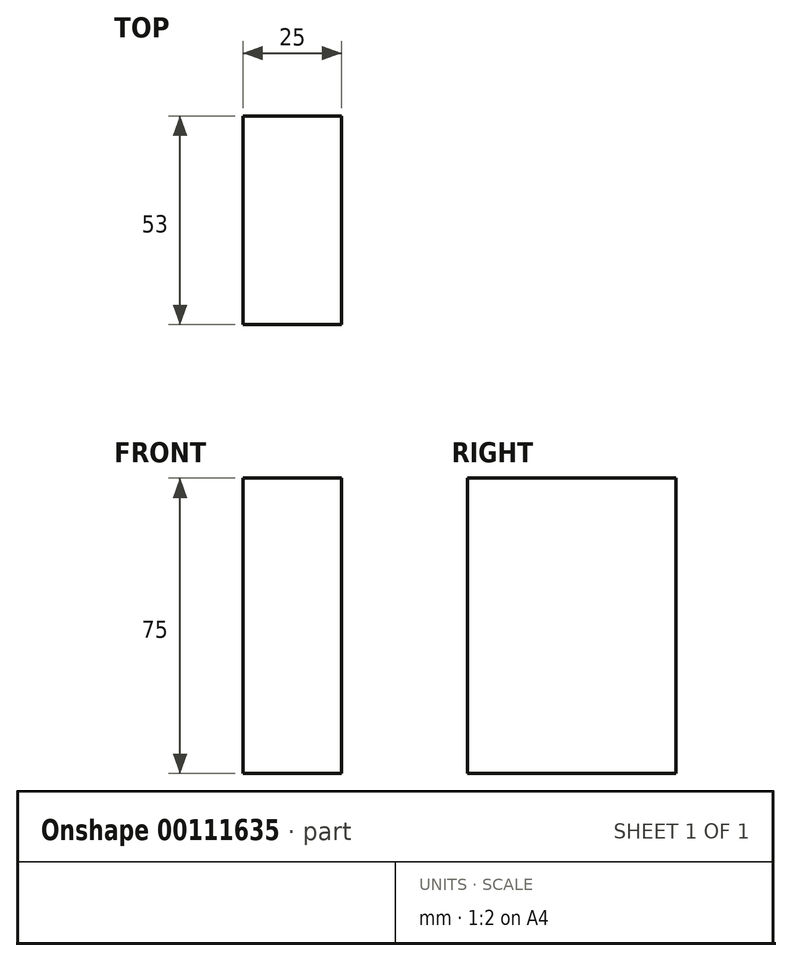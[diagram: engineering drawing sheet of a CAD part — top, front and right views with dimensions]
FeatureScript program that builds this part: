
annotation { "Feature Type Name" : "Feature", "Feature Type Description" : "" }
export const myFeature = defineFeature(function(context is Context, id is Id, definition is map)
    precondition{}
    {
        {
            var Q0;
            Q0=qCreatedBy(makeId("Front.planeOp"),FACE);
            var sketch = newSketch(context, id + "F0", { "sketchPlane" : qUnion([Q0])});
            skLineSegment(sketch, "E0.bottom", {"start": v(12.5, -37.5) * mm, "end": v(-12.5, -37.5) * mm});
            skLineSegment(sketch, "E0.top", {"start": v(12.5, 37.5) * mm, "end": v(-12.5, 37.5) * mm});
            skLineSegment(sketch, "E0.left", {"start": v(12.5, -37.5) * mm, "end": v(12.5, 37.5) * mm});
            skLineSegment(sketch, "E0.right", {"start": v(-12.5, -37.5) * mm, "end": v(-12.5, 37.5) * mm});
            skPoint(sketch, "E0.middle", {"position": v(0, 0) * mm});
            skSolve(sketch);
        }
        {
            var Q0;
            Q0 = qSketchRegion(id + "F0", true);
            extrude(context, id + "F1", {"entities" : qUnion([Q0]), "depth" : 53 * mm});
        }
    });
